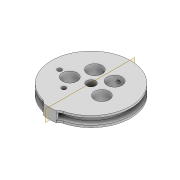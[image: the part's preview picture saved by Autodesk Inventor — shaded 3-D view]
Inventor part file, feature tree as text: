
AUTODESK INVENTOR PART (.ipt)
format: ipt  version: 2022 (Build 260153000, 153)  size: 318,976 bytes
history: native  units: mm
features: extrude x8, sketch x7, plane x3, fillet x2, mirror x2, pattern_circular x1, projected_geometry x1
ambient origin geometry x8: Origin, YZ Plane, XZ Plane, XY Plane, X Axis, Y Axis, Z Axis, Center Point
bodies: Solid1 (feature_tree)
feature tree (24):
  extrude  "Extrusion1"  Depth=32.0mm
  extrude  "Extrusion2"  Depth=3.0mm TaperAngle=0.0deg
  pattern_circular  "Circular Pattern1"  Count=5 Angle=360.0deg
  plane  "Work Plane1"
  plane  "Work Plane2"
  extrude  "Extrusion3"  [1 undecoded]
  extrude  "Extrusion4"  Depth=5.0mm
  fillet  "Fillet1"  Radius=2.5mm
  plane  "Work Plane3"
  extrude  "Extrusion5"  Depth=5.0mm TaperAngle=0.0deg
  mirror  "Mirror1"
  sketch  "Sketch6"  dims[d13=9.599311mm d14=-9.599311mm]
  extrude  "Extrusion6"  Depth=5.0mm
  extrude  "Extrusion7"  Depth=5.0mm
  extrude  "Extrusion8"  Depth=5.0mm
  fillet  "Fillet2"  Radius=10.0mm
  mirror  "Mirror2"
  sketch  "Sketch1"  dims[d0=4.2mm d2=32.0mm]
  sketch  "Sketch2"  dims[d3=4.0mm d4=3.0mm d5=0.0mm]
  sketch  "Sketch3"  dims[d6=7.0mm]
  sketch  "Sketch4"  dims[d7=8.0mm]
  sketch  "Sketch5"  dims[d8=10.0mm d9=0.0mm d10=50.0mm d11=360.0deg]
  projected_geometry  "Projected Loop1"
  sketch  "Sketch7"  dims[d15=1.5mm d16=1.5mm d17=2.5mm d18=5.0mm d19=0.0mm d20=1.5mm d21=1.5mm d22=2.5mm d23=10.0mm d24=0.0mm d25=1.0mm d26=37.4mm d27=1.0mm d28=0.0mm d29=2.1mm d30=13.0mm d31=1.9mm d32=2.1mm d33=8.4mm d35=5.0mm d36=0.0mm d37=100.0mm d38=0.0mm d39=4.5mm d40=3.0mm d41=3.0mm d42=1.0mm d43=5.0mm d44=0.0mm d45=3.0mm d46=10.0mm d47=0.0mm d48=5.0mm d49=0.0mm]
note: 1 required parameter value undecoded (feature->parameter linkage not recoverable at this tier; creation-order binding heuristic only, values carry confidence <= 0.55)
